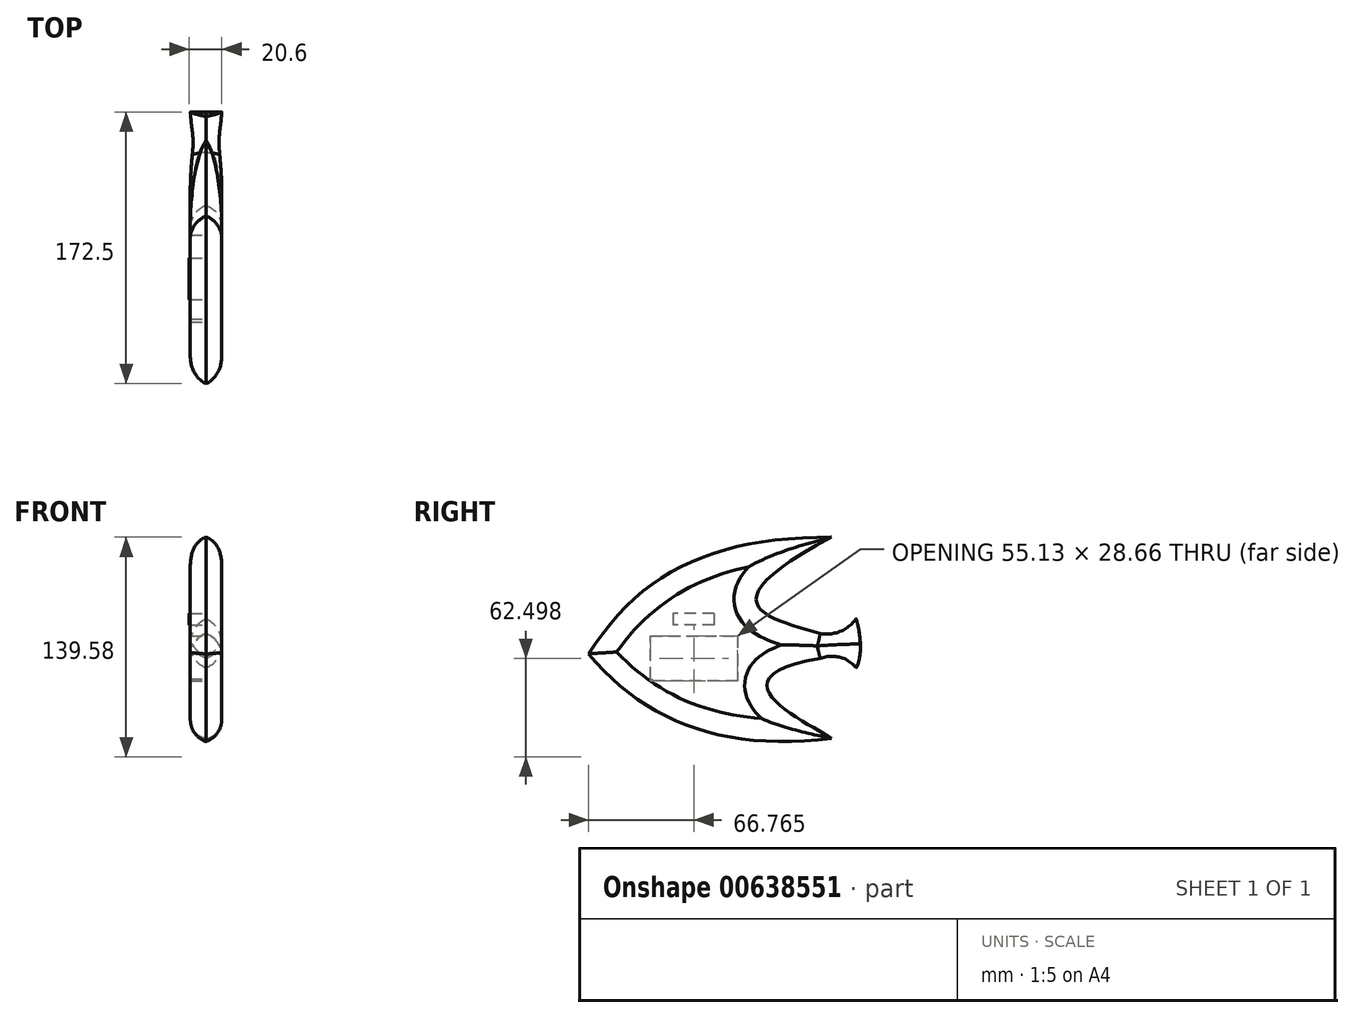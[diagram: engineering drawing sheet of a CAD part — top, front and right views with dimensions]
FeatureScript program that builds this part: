
annotation { "Feature Type Name" : "Feature", "Feature Type Description" : "" }
export const myFeature = defineFeature(function(context is Context, id is Id, definition is map)
    precondition{}
    {
        {
            var Q0;
            Q0=qCreatedBy(makeId("Right.planeOp"),FACE);
            var sketch = newSketch(context, id + "F0", { "sketchPlane" : qUnion([Q0])});
            skFitSpline(sketch, "E0", {"points": [v(-92.07, 0) * mm, v(62.17, 74.08) * mm], "startDerivative": vector(98.96, 158.42) * mm, "endDerivative": vector(219.93, -0.92) * mm});
            skFitSpline(sketch, "E1", {"points": [v(-92.08, 0.03) * mm, v(62.17, -53.81) * mm], "startDerivative": vector(106.79, -130.56) * mm, "endDerivative": vector(202.8, 25.35) * mm});
            skFitSpline(sketch, "E2", {"points": [v(62.17, 74.08) * mm, v(54.92, 12.9) * mm], "startDerivative": vector(-245.28, -129.49) * mm, "endDerivative": vector(102.08, -29.46) * mm});
            skFitSpline(sketch, "E3", {"points": [v(62.17, -53.81) * mm, v(54.92, -2.85) * mm], "startDerivative": vector(-47.27, 32.2) * mm, "endDerivative": vector(217.19, 37.68) * mm});
            skFitSpline(sketch, "E4", {"points": [v(54.92, 12.9) * mm, v(77.76, 22.27) * mm], "startDerivative": vector(28.1, -4.11) * mm, "endDerivative": vector(16.44, 22.6) * mm});
            skFitSpline(sketch, "E5", {"points": [v(77.76, 22.27) * mm, v(77.76, -8.8) * mm], "startDerivative": vector(12.33, -41.1) * mm, "endDerivative": vector(-8.9, -12.33) * mm});
            skFitSpline(sketch, "E6", {"points": [v(54.92, -2.85) * mm, v(77.76, -8.8) * mm], "startDerivative": vector(26.03, 8.56) * mm, "endDerivative": vector(17.81, -20.55) * mm});
            skSolve(sketch);
        }
        {
            var Q0;
            Q0=makeQuery(id+"F0.imprint","IMPRINT",FACE,{"disambiguationData":[TD([[makeQuery(id+"F0.imprint","IMPRINT",EDGE,{"derivedFrom":sQuery(id+"F0.wireOp",EDGE,"E0")}),-1.0]])]});
            extrude(context, id + "F1", {"entities" : qUnion([Q0]), "depth" : 10 * mm, "offsetDistance" : 25 * mm});
        }
        {
            var Q0;
            Q0=makeQuery(id+"F1.opExtrude","CAP_FACE",FACE,{"disambiguationData":[OSD([sQuery(id+"F0.wireOp",EDGE,"E0"),sQuery(id+"F0.wireOp",EDGE,"E1"),sQuery(id+"F0.wireOp",EDGE,"E2"),sQuery(id+"F0.wireOp",EDGE,"E3"),sQuery(id+"F0.wireOp",EDGE,"E4"),sQuery(id+"F0.wireOp",EDGE,"E5"),sQuery(id+"F0.wireOp",EDGE,"E6")])],"isStart":true});
            extrude(context, id + "F2", {"entities" : qUnion([Q0]), "depth" : 10 * mm, "offsetDistance" : 25 * mm});
        }
        {
            var Q0;
            Q0=makeQuery(id+"F1.opExtrude","CAP_EDGE",EDGE,{"disambiguationData":[OSD([sQuery(id+"F0.wireOp",EDGE,"E0")])],"isStart":false});
            var Q1;
            Q1=makeQuery(id+"F1.opExtrude","CAP_EDGE",EDGE,{"disambiguationData":[OSD([sQuery(id+"F0.wireOp",EDGE,"E1")])],"isStart":false});
            var Q2;
            Q2=makeQuery(id+"F1.opExtrude","CAP_EDGE",EDGE,{"disambiguationData":[OSD([sQuery(id+"F0.wireOp",EDGE,"E6")])],"isStart":false});
            var Q3;
            Q3=makeQuery(id+"F1.opExtrude","CAP_EDGE",EDGE,{"disambiguationData":[OSD([sQuery(id+"F0.wireOp",EDGE,"E3")])],"isStart":false});
            var Q4;
            Q4=makeQuery(id+"F1.opExtrude","CAP_EDGE",EDGE,{"disambiguationData":[OSD([sQuery(id+"F0.wireOp",EDGE,"E2")])],"isStart":false});
            var Q5;
            Q5=makeQuery(id+"F1.opExtrude","CAP_EDGE",EDGE,{"disambiguationData":[OSD([sQuery(id+"F0.wireOp",EDGE,"E4")])],"isStart":false});
            fillet(context, id + "F3", {"entities" : qUnion([Q0, Q1, Q2, Q3, Q4, Q5]), "radius" : 15 * mm, "tangentPropagation" : true, "allowEdgeOverflow" : false});
        }
        {
            var Q0;
            Q0=makeQuery(id+"F2.opExtrude","CAP_EDGE",EDGE,{"disambiguationData":[OSD([sQuery(id+"F0.wireOp",EDGE,"E0")])],"isStart":false});
            var Q1;
            Q1=makeQuery(id+"F2.opExtrude","CAP_EDGE",EDGE,{"disambiguationData":[OSD([sQuery(id+"F0.wireOp",EDGE,"E1")])],"isStart":false});
            var Q2;
            Q2=makeQuery(id+"F2.opExtrude","CAP_EDGE",EDGE,{"disambiguationData":[OSD([sQuery(id+"F0.wireOp",EDGE,"E3")])],"isStart":false});
            var Q3;
            Q3=makeQuery(id+"F2.opExtrude","CAP_EDGE",EDGE,{"disambiguationData":[OSD([sQuery(id+"F0.wireOp",EDGE,"E2")])],"isStart":false});
            var Q4;
            Q4=makeQuery(id+"F2.opExtrude","CAP_EDGE",EDGE,{"disambiguationData":[OSD([sQuery(id+"F0.wireOp",EDGE,"E4")])],"isStart":false});
            var Q5;
            Q5=makeQuery(id+"F2.opExtrude","CAP_EDGE",EDGE,{"disambiguationData":[OSD([sQuery(id+"F0.wireOp",EDGE,"E6")])],"isStart":false});
            fillet(context, id + "F4", {"entities" : qUnion([Q0, Q1, Q2, Q3, Q4, Q5]), "radius" : 15 * mm, "tangentPropagation" : true, "allowEdgeOverflow" : false});
        }
        {
            var Q0;
            Q0=qCreatedBy(makeId("Right.planeOp"),FACE);
            var sketch = newSketch(context, id + "F5", { "sketchPlane" : qUnion([Q0])});
            skLineSegment(sketch, "E7.top", {"start": v(0, -17.33) * mm, "end": v(-50.88, -17.33) * mm});
            skLineSegment(sketch, "E8", {"start": v(2.26, -17.33) * mm, "end": v(0, -17.33) * mm});
            skLineSegment(sketch, "E9", {"start": v(-50.88, -17.33) * mm, "end": v(-52.87, -15.85) * mm});
            skLineSegment(sketch, "E10", {"start": v(-52.87, -15.85) * mm, "end": v(-52.87, 11.33) * mm});
            skLineSegment(sketch, "E11", {"start": v(-52.87, 11.33) * mm, "end": v(2.26, 11.33) * mm});
            skLineSegment(sketch, "E12", {"start": v(2.26, 11.33) * mm, "end": v(2.26, -15.18) * mm});
            skLineSegment(sketch, "E13", {"start": v(2.26, -15.18) * mm, "end": v(2.26, -17.33) * mm});
            skSolve(sketch);
        }
        {
            var Q0;
            Q0 = qSketchRegion(id + "F5", true);
            extrude(context, id + "F6", {"entities" : qUnion([Q0]), "operationType" : NewBodyOperationType.REMOVE, "oppositeDirection" : true, "depth" : 60 * mm, "offsetDistance" : 25 * mm});
        }
        {
            var Q0;
            Q0=qCreatedBy(makeId("Right.planeOp"),FACE);
            var sketch = newSketch(context, id + "F7", { "sketchPlane" : qUnion([Q0])});
            skLineSegment(sketch, "E14.bottom", {"start": v(-12.43, 25.76) * mm, "end": v(-38.52, 25.76) * mm});
            skLineSegment(sketch, "E14.top", {"start": v(-12.43, 18.42) * mm, "end": v(-38.52, 18.42) * mm});
            skLineSegment(sketch, "E14.left", {"start": v(-12.43, 25.76) * mm, "end": v(-12.43, 18.42) * mm});
            skLineSegment(sketch, "E14.right", {"start": v(-38.52, 25.76) * mm, "end": v(-38.52, 18.42) * mm});
            skSolve(sketch);
        }
        {
            var Q0;
            Q0 = qSketchRegion(id + "F7", true);
            extrude(context, id + "F8", {"entities" : qUnion([Q0]), "oppositeDirection" : true, "depth" : 10.6 * mm, "offsetDistance" : 25 * mm});
        }
    });
